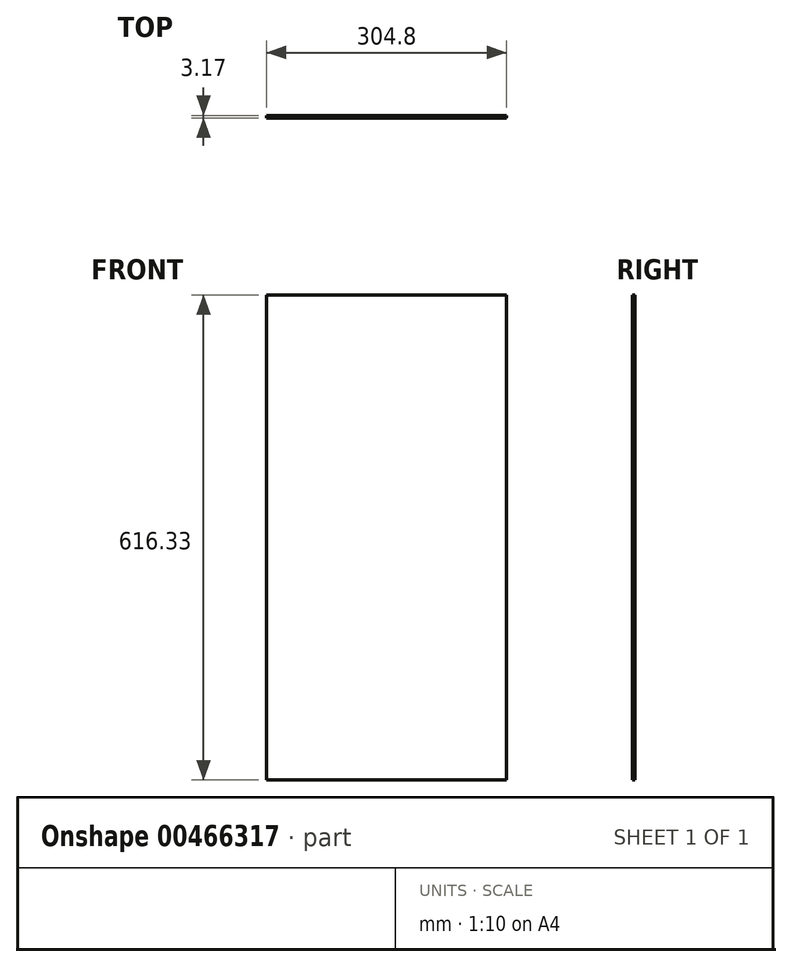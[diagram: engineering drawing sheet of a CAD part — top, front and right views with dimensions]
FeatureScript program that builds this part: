
annotation { "Feature Type Name" : "Feature", "Feature Type Description" : "" }
export const myFeature = defineFeature(function(context is Context, id is Id, definition is map)
    precondition{}
    {
        {
            var Q0;
            Q0=qCreatedBy(makeId("Front.planeOp"),FACE);
            var sketch = newSketch(context, id + "F0", { "sketchPlane" : qUnion([Q0])});
            skLineSegment(sketch, "E0.bottom", {"start": v(-118.87, 460.82) * mm, "end": v(185.93, 460.82) * mm});
            skLineSegment(sketch, "E0.top", {"start": v(-118.87, -155.5) * mm, "end": v(185.93, -155.5) * mm});
            skLineSegment(sketch, "E0.left", {"start": v(-118.87, 460.82) * mm, "end": v(-118.87, -155.5) * mm});
            skLineSegment(sketch, "E0.right", {"start": v(185.93, 460.82) * mm, "end": v(185.93, -155.5) * mm});
            skSolve(sketch);
        }
        {
            var Q0;
            Q0 = qSketchRegion(id + "F0", true);
            extrude(context, id + "F1", {"entities" : qUnion([Q0]), "depth" : 3.17 * mm});
        }
    });
